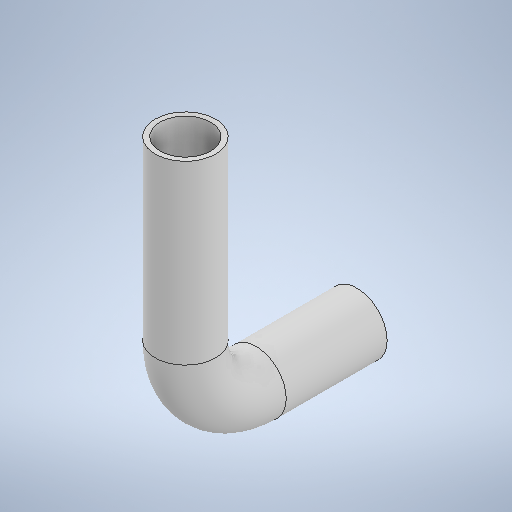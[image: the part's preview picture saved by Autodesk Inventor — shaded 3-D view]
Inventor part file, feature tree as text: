
AUTODESK INVENTOR PART (.ipt)
format: ipt  version: 2025.1 (Build 291241000, 241)  size: 281,600 bytes
history: native  units: mm
features: sketch x2, sweep x1
ambient origin geometry x8: Origin, YZ Plane, XZ Plane, XY Plane, X Axis, Y Axis, Z Axis, Center Point
bodies: Solid1 (feature_tree)
feature tree (3):
  sweep  "Sweep1"
  sketch  "Sketch1"  dims[d0=6.0mm d1=24.5mm]
  sketch  "Sketch2"  dims[d2=7.0mm d3=17.0mm d4=5.0mm d5=0.0mm d6=0.0mm]
